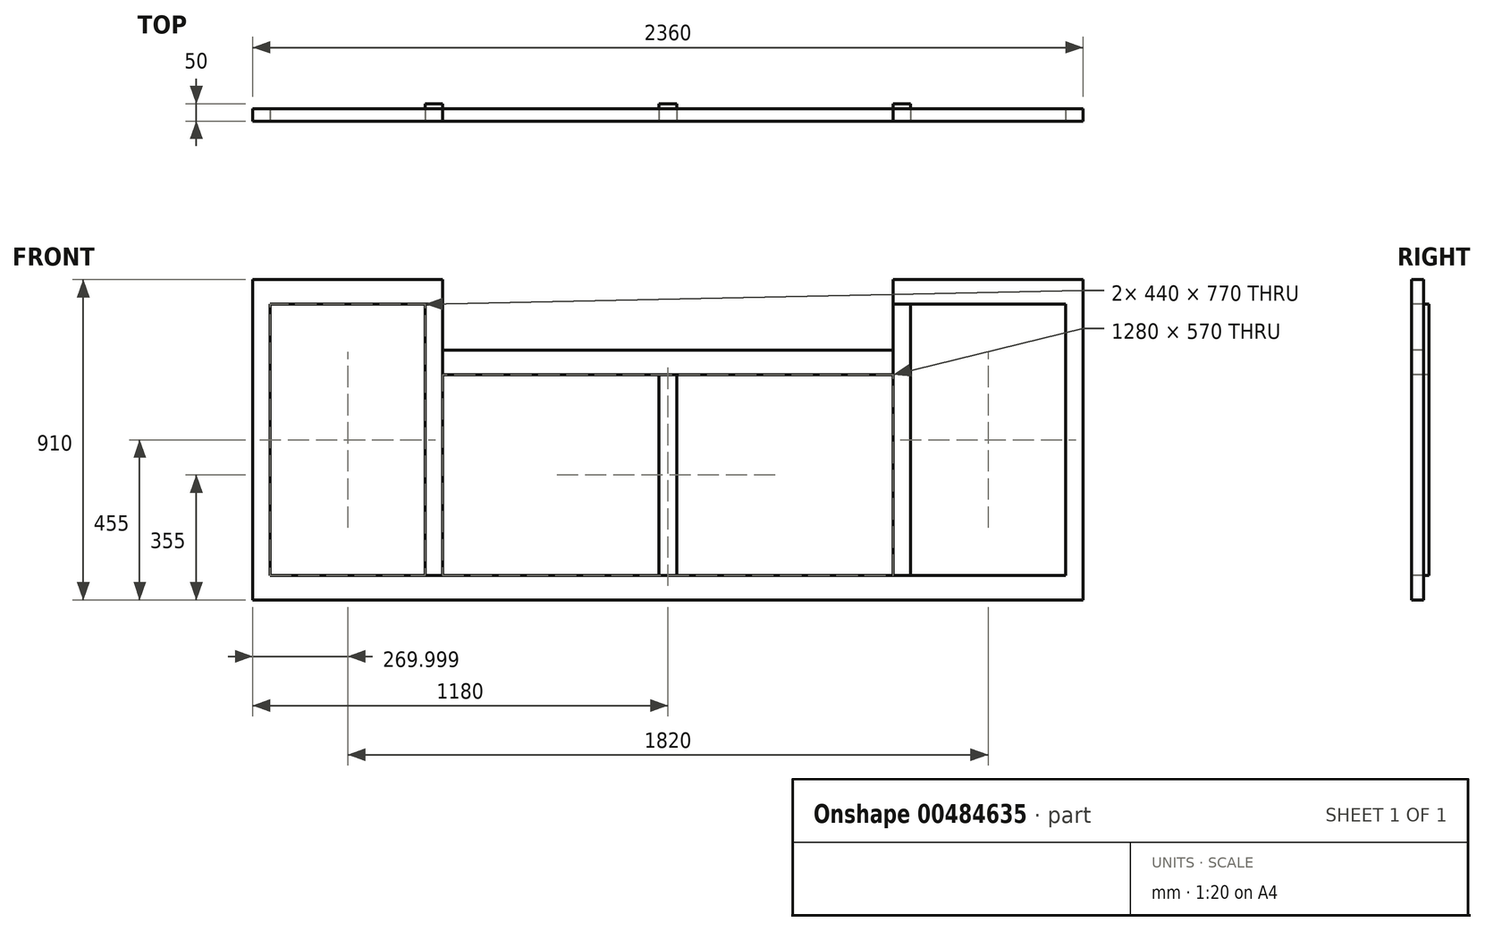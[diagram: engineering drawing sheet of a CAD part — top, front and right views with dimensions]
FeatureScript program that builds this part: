
annotation { "Feature Type Name" : "Feature", "Feature Type Description" : "" }
export const myFeature = defineFeature(function(context is Context, id is Id, definition is map)
    precondition{}
    {
        {
            var Q0;
            Q0=qCreatedBy(makeId("Front.planeOp"),FACE);
            var sketch = newSketch(context, id + "F0", { "sketchPlane" : qUnion([Q0])});
            skLineSegment(sketch, "E0.bottom", {"start": v(-540.64, 70) * mm, "end": v(739.36, 70) * mm});
            skLineSegment(sketch, "E0.top", {"start": v(-540.64, 0) * mm, "end": v(739.36, 0) * mm});
            skLineSegment(sketch, "E0.left", {"start": v(-540.64, 70) * mm, "end": v(-540.64, 0) * mm});
            skLineSegment(sketch, "E0.right", {"start": v(739.36, 70) * mm, "end": v(739.36, 0) * mm});
            skLineSegment(sketch, "E1.bottom", {"start": v(739.36, 200) * mm, "end": v(789.36, 200) * mm});
            skLineSegment(sketch, "E1.top", {"start": v(739.36, -570) * mm, "end": v(789.36, -570) * mm});
            skLineSegment(sketch, "E1.left", {"start": v(739.36, 200) * mm, "end": v(739.36, -570) * mm});
            skLineSegment(sketch, "E1.right", {"start": v(789.36, 200) * mm, "end": v(789.36, -570) * mm});
            skLineSegment(sketch, "E2.bottom", {"start": v(-540.64, 200) * mm, "end": v(-590.64, 200) * mm});
            skLineSegment(sketch, "E2.top", {"start": v(-540.64, -570) * mm, "end": v(-590.64, -570) * mm});
            skLineSegment(sketch, "E2.left", {"start": v(-540.64, 200) * mm, "end": v(-540.64, -570) * mm});
            skLineSegment(sketch, "E2.right", {"start": v(-590.64, 200) * mm, "end": v(-590.64, -570) * mm});
            skLineSegment(sketch, "E3.bottom", {"start": v(739.36, 200) * mm, "end": v(1279.36, 200) * mm});
            skLineSegment(sketch, "E3.top", {"start": v(739.36, 270) * mm, "end": v(1279.36, 270) * mm});
            skLineSegment(sketch, "E3.left", {"start": v(739.36, 200) * mm, "end": v(739.36, 270) * mm});
            skLineSegment(sketch, "E3.right", {"start": v(1279.36, 200) * mm, "end": v(1279.36, 270) * mm});
            skLineSegment(sketch, "E4.bottom", {"start": v(1279.36, 200) * mm, "end": v(1229.36, 200) * mm});
            skLineSegment(sketch, "E4.top", {"start": v(1279.36, -570) * mm, "end": v(1229.36, -570) * mm});
            skLineSegment(sketch, "E4.left", {"start": v(1279.36, 200) * mm, "end": v(1279.36, -570) * mm});
            skLineSegment(sketch, "E4.right", {"start": v(1229.36, 200) * mm, "end": v(1229.36, -570) * mm});
            skLineSegment(sketch, "E5.bottom", {"start": v(-540.64, 200) * mm, "end": v(-1080.64, 200) * mm});
            skLineSegment(sketch, "E5.top", {"start": v(-540.64, 270) * mm, "end": v(-1080.64, 270) * mm});
            skLineSegment(sketch, "E5.left", {"start": v(-540.64, 200) * mm, "end": v(-540.64, 270) * mm});
            skLineSegment(sketch, "E5.right", {"start": v(-1080.64, 200) * mm, "end": v(-1080.64, 270) * mm});
            skLineSegment(sketch, "E6.bottom", {"start": v(-1080.64, 200) * mm, "end": v(-1030.64, 200) * mm});
            skLineSegment(sketch, "E6.top", {"start": v(-1080.64, -570) * mm, "end": v(-1030.64, -570) * mm});
            skLineSegment(sketch, "E6.left", {"start": v(-1080.64, 200) * mm, "end": v(-1080.64, -570) * mm});
            skLineSegment(sketch, "E6.right", {"start": v(-1030.64, 200) * mm, "end": v(-1030.64, -570) * mm});
            skLineSegment(sketch, "E7.bottom", {"start": v(-1080.64, -570) * mm, "end": v(1279.36, -570) * mm});
            skLineSegment(sketch, "E7.top", {"start": v(-1080.64, -640) * mm, "end": v(1279.36, -640) * mm});
            skLineSegment(sketch, "E7.left", {"start": v(-1080.64, -570) * mm, "end": v(-1080.64, -640) * mm});
            skLineSegment(sketch, "E7.right", {"start": v(1279.36, -570) * mm, "end": v(1279.36, -640) * mm});
            skLineSegment(sketch, "E8", {"start": v(74.36, -570) * mm, "end": v(74.36, 0) * mm});
            skLineSegment(sketch, "E9", {"start": v(124.36, 0) * mm, "end": v(124.36, -570) * mm});
            skSolve(sketch);
        }
        {
            var Q0;
            {var subQ0=sQuery(id+"F0.wireOp",EDGE,"E8");Q0=makeQuery(id+"F0.imprint","IMPRINT",FACE,{"disambiguationData":[TD([[makeQuery(id+"F0.imprint","IMPRINT",EDGE,{"derivedFrom":subQ0}),-1.0]])]});}
            var Q1;
            {var subQ0=sQuery(id+"F0.wireOp",EDGE,"E1.right");Q1=makeQuery(id+"F0.imprint","IMPRINT",FACE,{"disambiguationData":[TD([[makeQuery(id+"F0.imprint","IMPRINT",EDGE,{"derivedFrom":subQ0}),-1.0]])]});}
            var Q2;
            Q2=makeQuery(id+"F0.imprint","IMPRINT",FACE,{"disambiguationData":[TD([[makeQuery(id+"F0.imprint","IMPRINT",EDGE,{"derivedFrom":sQuery(id+"F0.wireOp",EDGE,"E4.bottom")}),1.0]])]});
            var Q3;
            {var subQ0=sQuery(id+"F0.wireOp",EDGE,"E2.right");Q3=makeQuery(id+"F0.imprint","IMPRINT",FACE,{"disambiguationData":[TD([[makeQuery(id+"F0.imprint","IMPRINT",EDGE,{"derivedFrom":subQ0}),1.0]])]});}
            var Q4;
            Q4=makeQuery(id+"F0.imprint","IMPRINT",FACE,{"disambiguationData":[TD([[makeQuery(id+"F0.imprint","IMPRINT",EDGE,{"derivedFrom":sQuery(id+"F0.wireOp",EDGE,"E6.bottom")}),-1.0]])]});
            extrude(context, id + "F1", {"entities" : qUnion([Q0, Q1, Q2, Q3, Q4]), "oppositeDirection" : true, "depth" : 50 * mm});
        }
        {
            var Q0;
            Q0 = qSketchRegion(id + "F0", true);
            extrude(context, id + "F2", {"entities" : qUnion([Q0]), "oppositeDirection" : true, "depth" : 35 * mm});
        }
    });
